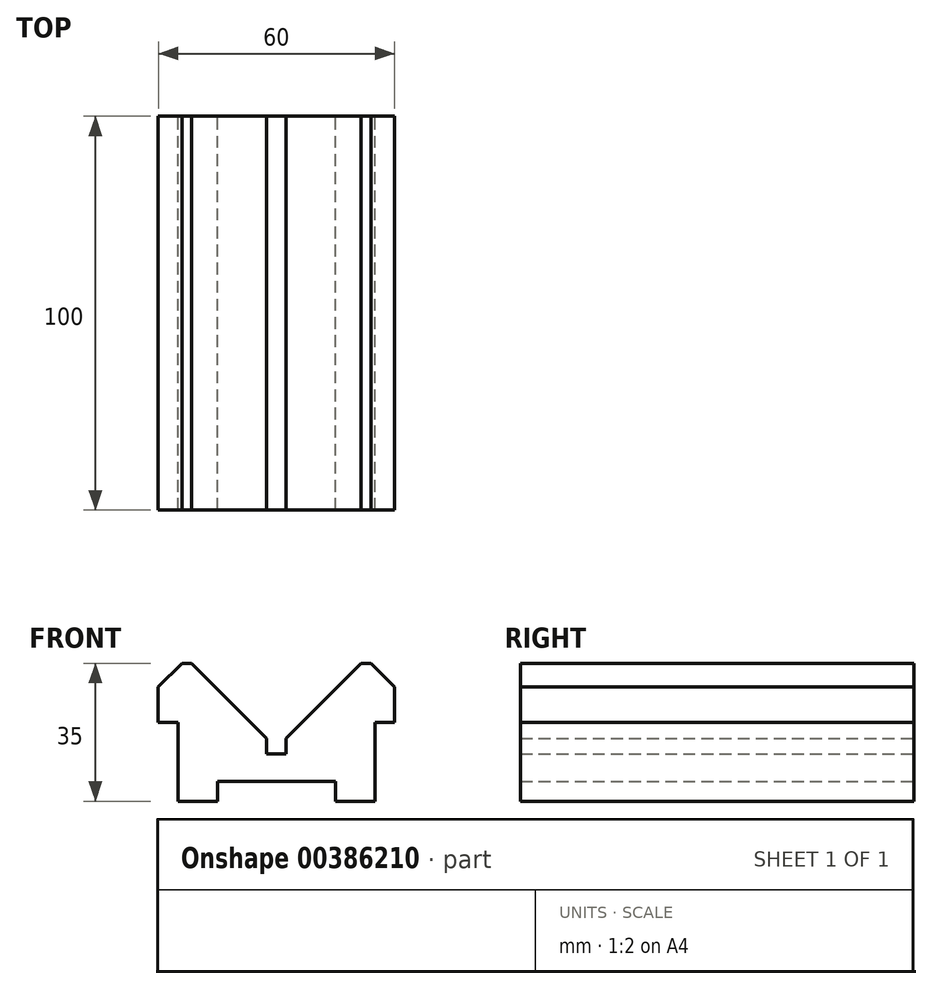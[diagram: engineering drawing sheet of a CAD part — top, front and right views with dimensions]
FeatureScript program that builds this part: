
annotation { "Feature Type Name" : "Feature", "Feature Type Description" : "" }
export const myFeature = defineFeature(function(context is Context, id is Id, definition is map)
    precondition{}
    {
        {
            var Q0;
            Q0=qCreatedBy(makeId("Front.planeOp"),FACE);
            var sketch = newSketch(context, id + "F0", { "sketchPlane" : qUnion([Q0])});
            skLineSegment(sketch, "E0.left", {"start": v(-31.1, 10.18) * mm, "end": v(-31.1, 1.18) * mm});
            skLineSegment(sketch, "E0.right", {"start": v(28.9, 10.18) * mm, "end": v(28.9, 1.18) * mm});
            skLineSegment(sketch, "E1.top", {"start": v(-31.1, 1.18) * mm, "end": v(-26.1, 1.18) * mm});
            skLineSegment(sketch, "E1.right", {"start": v(-26.1, -18.82) * mm, "end": v(-26.1, 1.18) * mm});
            skLineSegment(sketch, "E2.top", {"start": v(28.9, 1.18) * mm, "end": v(23.9, 1.18) * mm});
            skLineSegment(sketch, "E2.right", {"start": v(23.9, -18.82) * mm, "end": v(23.9, 1.18) * mm});
            skLineSegment(sketch, "E3", {"start": v(28.9, 10.18) * mm, "end": v(22.9, 16.18) * mm});
            skLineSegment(sketch, "E4", {"start": v(-31.1, 10.18) * mm, "end": v(-25.1, 16.18) * mm});
            skLineSegment(sketch, "E5.bottom", {"start": v(-16.1, -13.82) * mm, "end": v(13.9, -13.82) * mm});
            skLineSegment(sketch, "E5.left", {"start": v(-16.1, -13.82) * mm, "end": v(-16.1, -18.82) * mm});
            skLineSegment(sketch, "E5.right", {"start": v(13.9, -13.82) * mm, "end": v(13.9, -18.82) * mm});
            skLineSegment(sketch, "E6.trimOffspring", {"start": v(13.9, -18.82) * mm, "end": v(23.9, -18.82) * mm});
            skLineSegment(sketch, "E7", {"start": v(-26.1, -18.82) * mm, "end": v(-16.1, -18.82) * mm});
            skLineSegment(sketch, "E8.bottom", {"start": v(1.4, -6.82) * mm, "end": v(-3.6, -6.82) * mm});
            skLineSegment(sketch, "E8.left", {"start": v(1.4, -6.82) * mm, "end": v(1.4, -2.82) * mm});
            skLineSegment(sketch, "E8.right", {"start": v(-3.6, -6.82) * mm, "end": v(-3.6, -2.82) * mm});
            skLineSegment(sketch, "E9", {"start": v(-25.1, 16.18) * mm, "end": v(-22.6, 16.18) * mm});
            skLineSegment(sketch, "E10", {"start": v(20.4, 16.18) * mm, "end": v(22.9, 16.18) * mm});
            skPoint(sketch, "E11.orphan", {"position": v(20.4, 16.18) * mm});
            skLineSegment(sketch, "E12", {"start": v(1.4, -2.82) * mm, "end": v(20.4, 16.18) * mm});
            skPoint(sketch, "E13.bottom.end.orphan", {"position": v(1.4, 16.18) * mm});
            skLineSegment(sketch, "E14", {"start": v(-22.6, 16.18) * mm, "end": v(-3.6, -2.82) * mm});
            skSolve(sketch);
        }
        {
            var Q0;
            Q0 = qSketchRegion(id + "F0", true);
            extrude(context, id + "F1", {"entities" : qUnion([Q0]), "depth" : 100 * mm});
        }
    });
